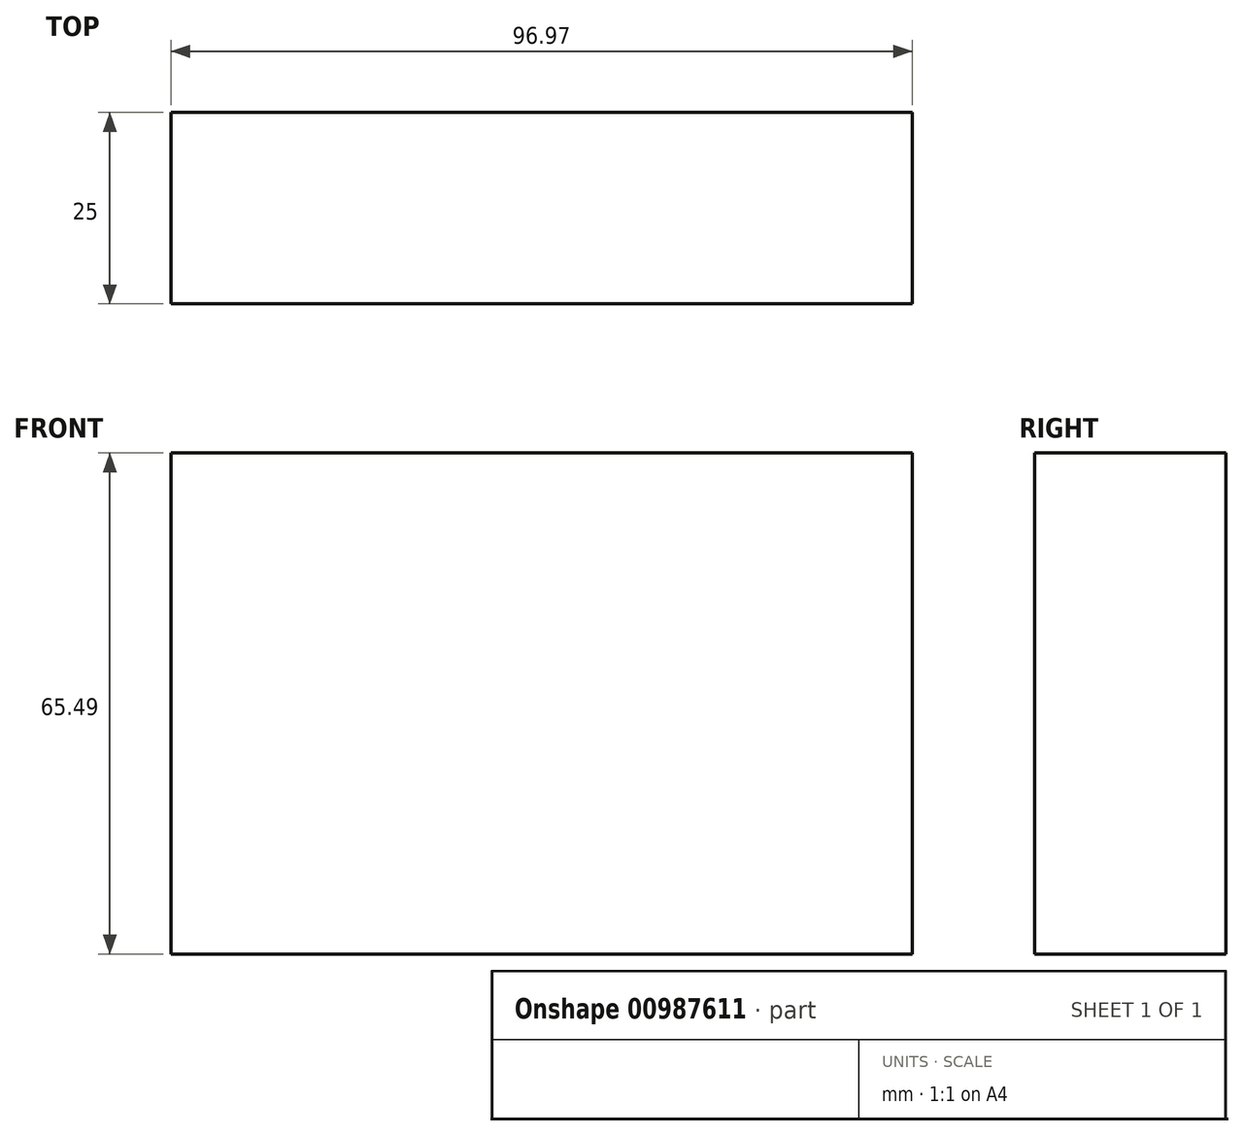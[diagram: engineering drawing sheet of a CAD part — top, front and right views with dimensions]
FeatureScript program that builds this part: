
annotation { "Feature Type Name" : "Feature", "Feature Type Description" : "" }
export const myFeature = defineFeature(function(context is Context, id is Id, definition is map)
    precondition{}
    {
        {
            var Q0;
            Q0=qCreatedBy(makeId("Front.planeOp"),FACE);
            var sketch = newSketch(context, id + "F0", { "sketchPlane" : qUnion([Q0])});
            skLineSegment(sketch, "E0.bottom", {"start": v(-42.86, 26.84) * mm, "end": v(54.1, 26.84) * mm});
            skLineSegment(sketch, "E0.top", {"start": v(-42.86, -38.65) * mm, "end": v(54.1, -38.65) * mm});
            skLineSegment(sketch, "E0.left", {"start": v(-42.86, 26.84) * mm, "end": v(-42.86, -38.65) * mm});
            skLineSegment(sketch, "E0.right", {"start": v(54.1, 26.84) * mm, "end": v(54.1, -38.65) * mm});
            skSolve(sketch);
        }
        {
            var Q0;
            Q0 = qSketchRegion(id + "F0", true);
            extrude(context, id + "F1", {"entities" : qUnion([Q0]), "depth" : 25 * mm, "offsetDistance" : 25 * mm});
        }
    });
